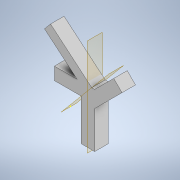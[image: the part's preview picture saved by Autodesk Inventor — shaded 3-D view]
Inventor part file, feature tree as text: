
AUTODESK INVENTOR PART (.ipt)
format: ipt  version: 2021.1 (Build 251245000, 245)  size: 131,072 bytes
history: native  units: in
note: dims shown in document units (in); Inventor stores cm internally (conversion verified against a paired STEP export)
features: sketch x5, extrude x4, plane x1
ambient origin geometry x8: Origin, YZ Plane, XZ Plane, XY Plane, X Axis, Y Axis, Z Axis, Center Point
bodies: Solid1 (feature_tree)
feature tree (10):
  extrude  "Extrusion1"  Depth=4.0in TaperAngle=0.0deg
  extrude  "Extrusion3"  Depth=2.0in
  extrude  "Extrusion4"  Depth=1.0in TaperAngle=0.0deg
  plane  "Work Plane2"
  extrude  "Extrusion6"  Depth=4.0in TaperAngle=0.0deg
  sketch  "Sketch7"
  sketch  "Sketch1"  dims[d0=1.0in d1=4.0in d2=0.0in]
  sketch  "Sketch3"  dims[d5=2.0in d6=0.0in d7=2.0in]
  sketch  "Sketch4"  dims[d8=45.0deg d9=1.0in d10=0.0in]
  sketch  "Sketch6"  dims[d14=0.2749in d15=4.0in d16=0.0in]
